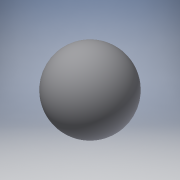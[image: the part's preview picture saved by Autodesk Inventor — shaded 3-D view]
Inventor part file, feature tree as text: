
AUTODESK INVENTOR PART (.ipt)
format: ipt  version: 2016 (Build 200138000, 138)  size: 117,760 bytes
history: native  units: in
note: dims shown in document units (in); Inventor stores cm internally (conversion verified against a paired STEP export)
features: revolve x1, sketch x1
ambient origin geometry x8: Origin, YZ Plane, XZ Plane, XY Plane, X Axis, Y Axis, Z Axis, Center Point
bodies: Solid1 (feature_tree)
feature tree (2):
  revolve  "Revolution1"  [1 undecoded]
  sketch  "Sketch1"  dims[d0=10.0in d2=5.0in d3=90.0deg]
note: 1 required parameter value undecoded (feature->parameter linkage not recoverable at this tier; creation-order binding heuristic only, values carry confidence <= 0.55)
